# Revit family: CWM-Surface_Mount
name_source: partatom
category: Lighting Fixtures
units: mm (PartAtom-declared; Revit-internal decimal feet)

## family parameters
Cut with Voids When Loaded = No
Host = Face
Light Source = Yes
OmniClass Number = 23.80.70.11
OmniClass Title = Luminaries for Internal Lighting
Part Type = Normal
Room Calculation Point = No
Round Connector Dimension = Use Diameter
Shared = No

## types (2) — shared parameters
Apparent Load = 0 VA
Backbox = Paint-White
Color Filter = 16777215
Default Elevation = 48 "
Description = Contemporary LED Wall Mount
Dimming Lamp Color Temperature Shift = <None>
Driver = Fixed Output
Emit Shape Visible in Rendering = No
Emit from Rectangle Width = 4.5 "
Glass = Glass
Lamp = LED Lamp
Load Classification = Lighting
Lumen Output = Medium Lumen
Manufacturer = Columbia Lighting
Model = CWM
Nominal Watts = 38 W
Photometric Notes = Photometric web download in link
Tilt Angle = -90.00°
URL = https://www.currentlighting.com
Voltage = 120 V
Wattage Comments = 17-38 W

## per-type parameters (varying)
| type | Emit from Rectangle Length | Photometric Web File | Row Length |
| CWM 4' | 44.5 " | CWM4-30MLxx-SByy-EDU.ies | 48 " |
| CWM 2' | 20.5 " | CWM2-30LWxx-FRyy-EDU.ies | 24 " |

## geometry (parser evidence)
native form markers: Sweep x3
no freeform markers — native parametric forms only
